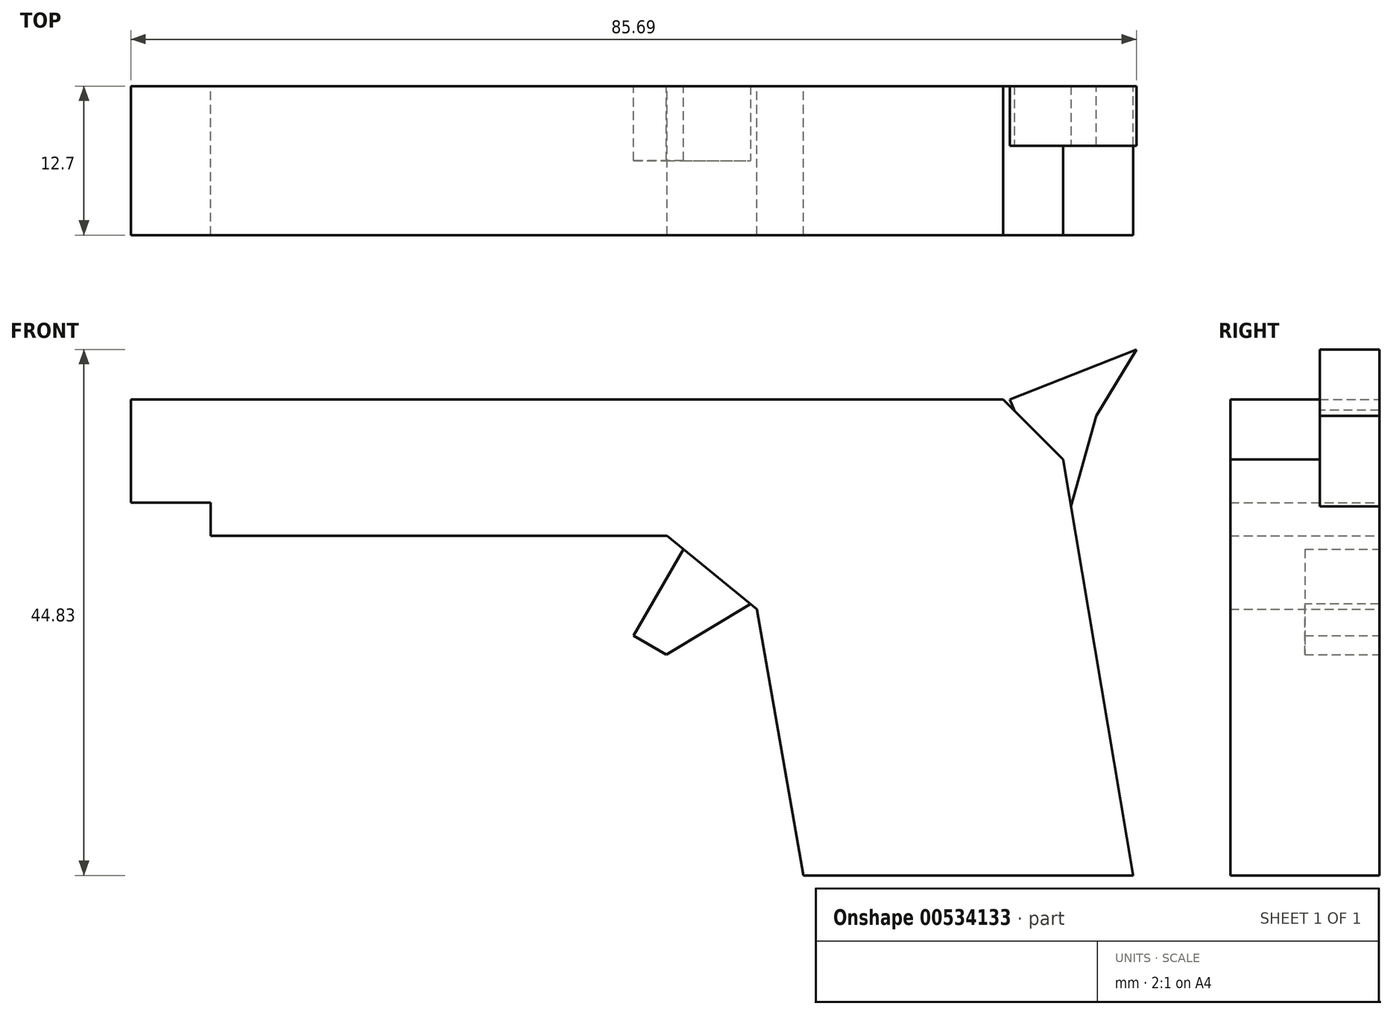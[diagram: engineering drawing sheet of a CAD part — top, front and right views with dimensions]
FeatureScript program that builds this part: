
annotation { "Feature Type Name" : "Feature", "Feature Type Description" : "" }
export const myFeature = defineFeature(function(context is Context, id is Id, definition is map)
    precondition{}
    {
        {
            var Q0;
            Q0=qCreatedBy(makeId("Front.planeOp"),FACE);
            var sketch = newSketch(context, id + "F0", { "sketchPlane" : qUnion([Q0])});
            skLineSegment(sketch, "E0", {"start": v(27.66, 0) * mm, "end": v(55.75, 0) * mm});
            skLineSegment(sketch, "E1", {"start": v(55.75, 0) * mm, "end": v(49.8, 35.47) * mm});
            skLineSegment(sketch, "E2", {"start": v(49.8, 35.47) * mm, "end": v(44.69, 40.57) * mm});
            skLineSegment(sketch, "E3", {"start": v(44.69, 40.57) * mm, "end": v(-29.65, 40.57) * mm});
            skLineSegment(sketch, "E4", {"start": v(-29.65, 40.57) * mm, "end": v(-29.65, 31.78) * mm});
            skLineSegment(sketch, "E5", {"start": v(-29.65, 31.78) * mm, "end": v(-22.84, 31.78) * mm});
            skLineSegment(sketch, "E6", {"start": v(-22.84, 31.78) * mm, "end": v(-22.84, 28.94) * mm});
            skLineSegment(sketch, "E7", {"start": v(-22.84, 28.94) * mm, "end": v(16.03, 28.94) * mm});
            skLineSegment(sketch, "E8", {"start": v(16.03, 28.94) * mm, "end": v(23.7, 22.7) * mm});
            skLineSegment(sketch, "E9", {"start": v(23.7, 22.7) * mm, "end": v(27.66, 0) * mm});
            skSolve(sketch);
        }
        {
            var Q0;
            Q0=makeQuery(id+"F0.imprint","IMPRINT",FACE,{"disambiguationData":[TD([[makeQuery(id+"F0.imprint","IMPRINT",EDGE,{"derivedFrom":sQuery(id+"F0.wireOp",EDGE,"E0")}),1.0]])]});
            extrude(context, id + "F1", {"entities" : qUnion([Q0]), "depth" : 12.7 * mm, "offsetDistance" : 25.4 * mm});
        }
        {
            var Q0;
            Q0=qCreatedBy(makeId("Front.planeOp"),FACE);
            var sketch = newSketch(context, id + "F2", { "sketchPlane" : qUnion([Q0])});
            skLineSegment(sketch, "E10", {"start": v(45.25, 40.57) * mm, "end": v(56.04, 44.83) * mm});
            skLineSegment(sketch, "E11", {"start": v(56.04, 44.83) * mm, "end": v(52.63, 39.15) * mm});
            skLineSegment(sketch, "E12", {"start": v(52.63, 39.15) * mm, "end": v(50.08, 30.07) * mm});
            skLineSegment(sketch, "E13", {"start": v(45.25, 40.57) * mm, "end": v(47.6, 34.61) * mm});
            skPoint(sketch, "E13.endSnap0", {"position": v(51.35, 34.61) * mm});
            skLineSegment(sketch, "E14", {"start": v(47.6, 34.61) * mm, "end": v(50.08, 30.07) * mm});
            skSolve(sketch);
        }
        {
            var Q0;
            Q0=makeQuery(id+"F2.imprint","IMPRINT",FACE,{"disambiguationData":[TD([[makeQuery(id+"F2.imprint","IMPRINT",EDGE,{"derivedFrom":sQuery(id+"F2.wireOp",EDGE,"E10")}),-1.0]])]});
            extrude(context, id + "F3", {"entities" : qUnion([Q0]), "operationType" : NewBodyOperationType.ADD, "depth" : 5.08 * mm, "offsetDistance" : 25.4 * mm});
        }
        {
            var Q0;
            Q0=qCreatedBy(makeId("Front.planeOp"),FACE);
            var sketch = newSketch(context, id + "F4", { "sketchPlane" : qUnion([Q0])});
            skLineSegment(sketch, "E15", {"start": v(17.45, 27.8) * mm, "end": v(13.2, 20.43) * mm});
            skLineSegment(sketch, "E16", {"start": v(13.2, 20.43) * mm, "end": v(15.97, 18.83) * mm});
            skLineSegment(sketch, "E17", {"start": v(15.97, 18.83) * mm, "end": v(23.4, 23.27) * mm});
            skLineSegment(sketch, "E18", {"start": v(17.45, 27.8) * mm, "end": v(23.4, 23.27) * mm});
            skSolve(sketch);
        }
        {
            var Q0;
            Q0=makeQuery(id+"F4.imprint","IMPRINT",FACE,{"disambiguationData":[TD([[makeQuery(id+"F4.imprint","IMPRINT",EDGE,{"derivedFrom":sQuery(id+"F4.wireOp",EDGE,"E15")}),1.0]])]});
            extrude(context, id + "F5", {"entities" : qUnion([Q0]), "operationType" : NewBodyOperationType.ADD, "depth" : 6.35 * mm, "offsetDistance" : 25.4 * mm});
        }
    });
